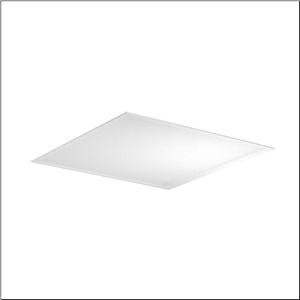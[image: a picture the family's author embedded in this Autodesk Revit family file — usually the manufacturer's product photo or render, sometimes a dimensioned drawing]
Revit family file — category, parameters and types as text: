
# Revit family: apollon_r__31_square_51mp12wd2n42_b6b6
name_source: partatom
category: Lighting Fixtures
units: mm (PartAtom-declared; Revit-internal decimal feet)

## family parameters
Cut with Voids When Loaded = No
Host = Face
Light Source = No
Part Type = Normal
Room Calculation Point = No
Round Connector Dimension = Use Diameter
Shared = No

## types (1)
- --- (1 x LED, 4000 lm, 27.5 W, 5000K)
    Apparent Load = 28 VA
    CIE Flux Codes = 62 87 97 100 100
    Color Rendering = 80
    Color Temperature = 5000K
    Default Elevation = 1800 mm
    Description = Apollon® 31 square, office luminaire, primary optical cover: micro prismatic cover, of PMMA, CAT 2 (L<= 3000cd/m²), light emission: direct distribution, primary light characteristic: symmetric, installation type: lay-in mounting, LED, rated luminous flux: 4.000lm, luminous efficacy: 145lm/W, light colour: 840/850, colour temperature: 4000/5000K, with terminal, 5-pole, mains connection: 220..240V, AC/DC, 0/50..60Hz, rated input power: 28W, housing, of aluminium, traffic white (RAL 9016), module: M600, length: 595mm, width: 595mm, height: 32mm, housing upper side, of sheet steel, galvanised, protection rating (complete): IP20, protection rating (on room side): IP40, insulation class (complete): insulation class II (safety insulation), certification: CE, ENEC, impact resistance: IK03, permissible operating ambient temperature: -20..+40°C, permissible storage temperature: -20..+60°C, packaging unit: 1 piece
    Height = 0 mm  [stored 0 ft]
    Lamp = 1 x LED
    Lamp Light Flux = 4000 lm
    Lamp Power = 27.5 W
    Lamp count = 1
    Length = 595 mm
    Luminous efficacy = 145 lm/W
    Manufacturer = Siteco
    ModVariant = No
    Model = 51MP12WD2N42
    Mounting Place = Ceiling
    Mounting Type = Recessed
    Number of Poles = 1
    OnlyDefault = Yes
    Power Factor = 1
    Product Name = Apollon® 31 square
    Product group = office luminaire | ceiling recessed
    ProductGroupID = 401
    Protection Class = Protection class II
    Protection Degree = IP 20
    RLX_Detail_Level = 1
    RLX_Emergency_Light_Flux = 0 lm
    RLX_Emergency_Type = 0
    RLX_Emergency_Type_DB = No
    RlxData = <blob elided: 12689 chars, md5=df466c47>
    Socket = socket
    Standby Power = 0 W
    System Light Flux = 4000 lm
    System Power = 28 W
    Type Comments = individual setting: colour temperature 5000K
    Type Image = l_1291035.jpg
    URL = http://relux.com
    VarID = @adj_027777
    Voltage = 0 V
    Weight = 0.00 kg
    Width = 595 mm

note: [stored X ft] marks values corroborated as IEEE doubles in the binary element streams (Revit-internal decimal feet)

## geometry (parser evidence)
native form markers: Sweep x11
no freeform markers — native parametric forms only
